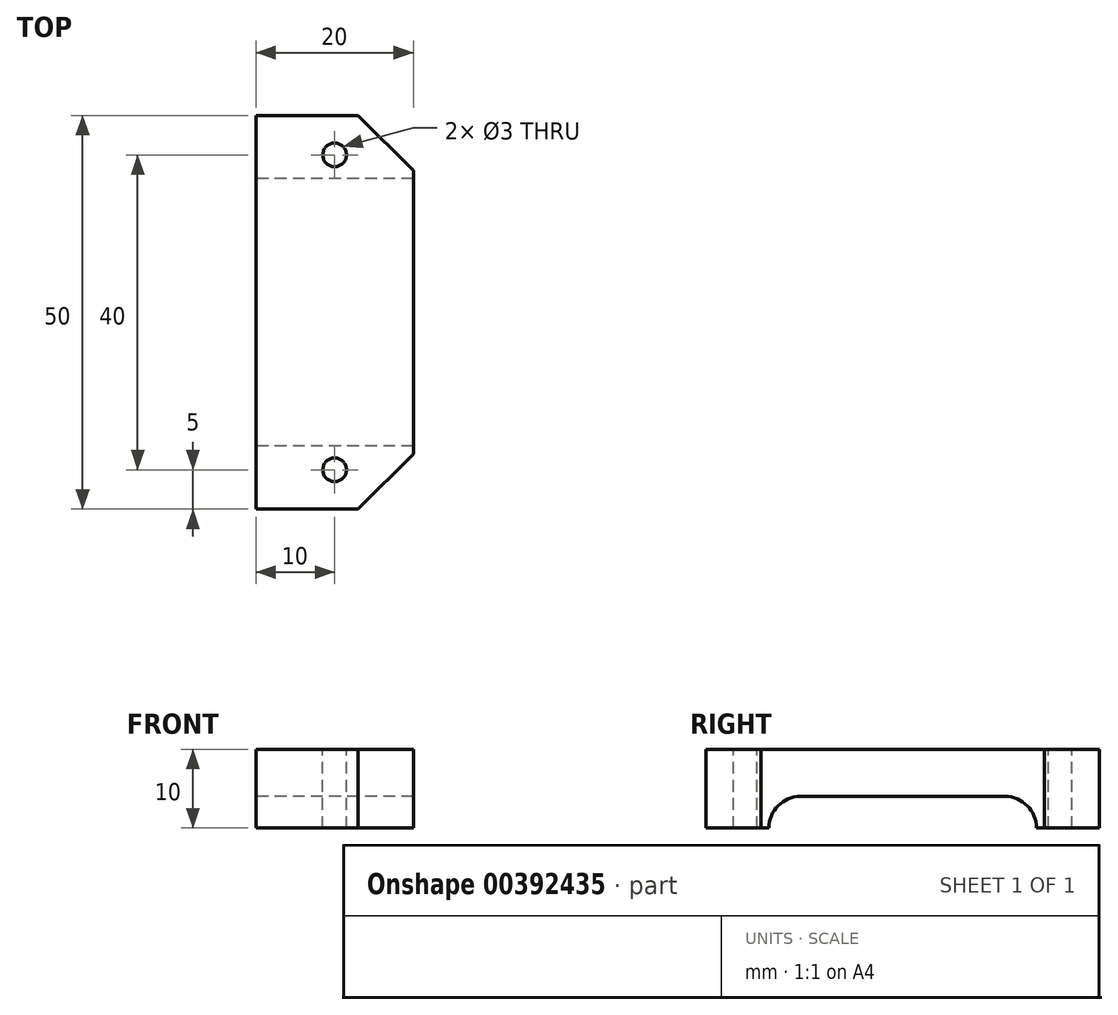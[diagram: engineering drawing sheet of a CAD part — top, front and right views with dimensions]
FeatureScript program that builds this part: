
annotation { "Feature Type Name" : "Feature", "Feature Type Description" : "" }
export const myFeature = defineFeature(function(context is Context, id is Id, definition is map)
    precondition{}
    {
        {
            var Q0;
            Q0=qCreatedBy(makeId("Top.planeOp"),FACE);
            var sketch = newSketch(context, id + "F0", { "sketchPlane" : qUnion([Q0])});
            skLineSegment(sketch, "E0.bottom", {"start": v(0, 0) * mm, "end": v(20, 0) * mm});
            skLineSegment(sketch, "E0.top", {"start": v(0, 50) * mm, "end": v(20, 50) * mm});
            skLineSegment(sketch, "E0.left", {"start": v(0, 0) * mm, "end": v(0, 50) * mm});
            skLineSegment(sketch, "E0.right", {"start": v(20, 0) * mm, "end": v(20, 50) * mm});
            skSolve(sketch);
        }
        {
            var Q0;
            Q0=qSketchRegion(id+"F0",true);
            extrude(context, id + "F1", {"entities" : qUnion([Q0]), "depth" : 10 * mm});
        }
        {
            var Q0;
            Q0=makeQuery(id+"F1.opExtrude","CAP_FACE",FACE,{"disambiguationData":[OSD([sQuery(id+"F0.wireOp",EDGE,"E0.bottom"),sQuery(id+"F0.wireOp",EDGE,"E0.top"),sQuery(id+"F0.wireOp",EDGE,"E0.left"),sQuery(id+"F0.wireOp",EDGE,"E0.right")])],"isStart":false});
            var sketch = newSketch(context, id + "F2", { "sketchPlane" : qUnion([Q0])});
            skCircle(sketch, "E1", {"center": v(10, 45) * mm, "radius": 1.5 * mm});
            skCircle(sketch, "E2", {"center": v(10, 5) * mm, "radius": 1.5 * mm});
            skSolve(sketch);
        }
        {
            var Q0;
            Q0=qSketchRegion(id+"F2",true);
            extrude(context, id + "F3", {"entities" : qUnion([Q0]), "operationType" : NewBodyOperationType.REMOVE, "endBound" : BoundingType.THROUGH_ALL, "oppositeDirection" : true, "depth" : 25 * mm});
        }
        {
            var Q0;
            Q0=makeQuery(id+"F1.opExtrude","SWEPT_FACE",FACE,{"disambiguationData":[OSD([sQuery(id+"F0.wireOp",EDGE,"E0.left")])]});
            var sketch = newSketch(context, id + "F4", { "sketchPlane" : qUnion([Q0])});
            skArc(sketch, "E3", {"start": v(-8, 0) * mm, "mid": v(-9.17, 2.83) * mm, "end": v(-12, 4) * mm});
            skArc(sketch, "E4", {"start": v(-42, 0) * mm, "mid": v(-40.83, 2.83) * mm, "end": v(-38, 4) * mm});
            skLineSegment(sketch, "E5", {"start": v(-12, 4) * mm, "end": v(-38, 4) * mm});
            skLineSegment(sketch, "E6", {"start": v(-42, 0) * mm, "end": v(-8, 0) * mm});
            skSolve(sketch);
        }
        {
            var Q0;
            Q0=qSketchRegion(id+"F4",true);
            extrude(context, id + "F5", {"entities" : qUnion([Q0]), "operationType" : NewBodyOperationType.REMOVE, "endBound" : BoundingType.THROUGH_ALL, "oppositeDirection" : true, "depth" : 25 * mm});
        }
        {
            var Q0;
            Q0=makeQuery(id+"F1.opExtrude","CAP_FACE",FACE,{"disambiguationData":[OSD([sQuery(id+"F0.wireOp",EDGE,"E0.bottom"),sQuery(id+"F0.wireOp",EDGE,"E0.top"),sQuery(id+"F0.wireOp",EDGE,"E0.left"),sQuery(id+"F0.wireOp",EDGE,"E0.right")])],"isStart":false});
            var sketch = newSketch(context, id + "F6", { "sketchPlane" : qUnion([Q0])});
            skLineSegment(sketch, "E7", {"start": v(20, 0) * mm, "end": v(20, 7) * mm});
            skLineSegment(sketch, "E8", {"start": v(20, 7) * mm, "end": v(13, 0) * mm});
            skLineSegment(sketch, "E9", {"start": v(13, 0) * mm, "end": v(20, 0) * mm});
            skLineSegment(sketch, "E10", {"start": v(20, 50) * mm, "end": v(20, 43) * mm});
            skLineSegment(sketch, "E11", {"start": v(20, 43) * mm, "end": v(13, 50) * mm});
            skLineSegment(sketch, "E12", {"start": v(13, 50) * mm, "end": v(20, 50) * mm});
            skSolve(sketch);
        }
        {
            var Q0;
            Q0=makeQuery(id+"F6.imprint","IMPRINT",FACE,{"disambiguationData":[TD([[makeQuery(id+"F6.imprint","IMPRINT",EDGE,{"derivedFrom":sQuery(id+"F6.wireOp",EDGE,"E7")}),1.0]])]});
            var Q1;
            Q1=makeQuery(id+"F6.imprint","IMPRINT",FACE,{"disambiguationData":[TD([[makeQuery(id+"F6.imprint","IMPRINT",EDGE,{"derivedFrom":sQuery(id+"F6.wireOp",EDGE,"E10")}),1.0]])]});
            extrude(context, id + "F7", {"entities" : qUnion([Q0, Q1]), "operationType" : NewBodyOperationType.REMOVE, "endBound" : BoundingType.THROUGH_ALL, "oppositeDirection" : true, "depth" : 25 * mm});
        }
    });
